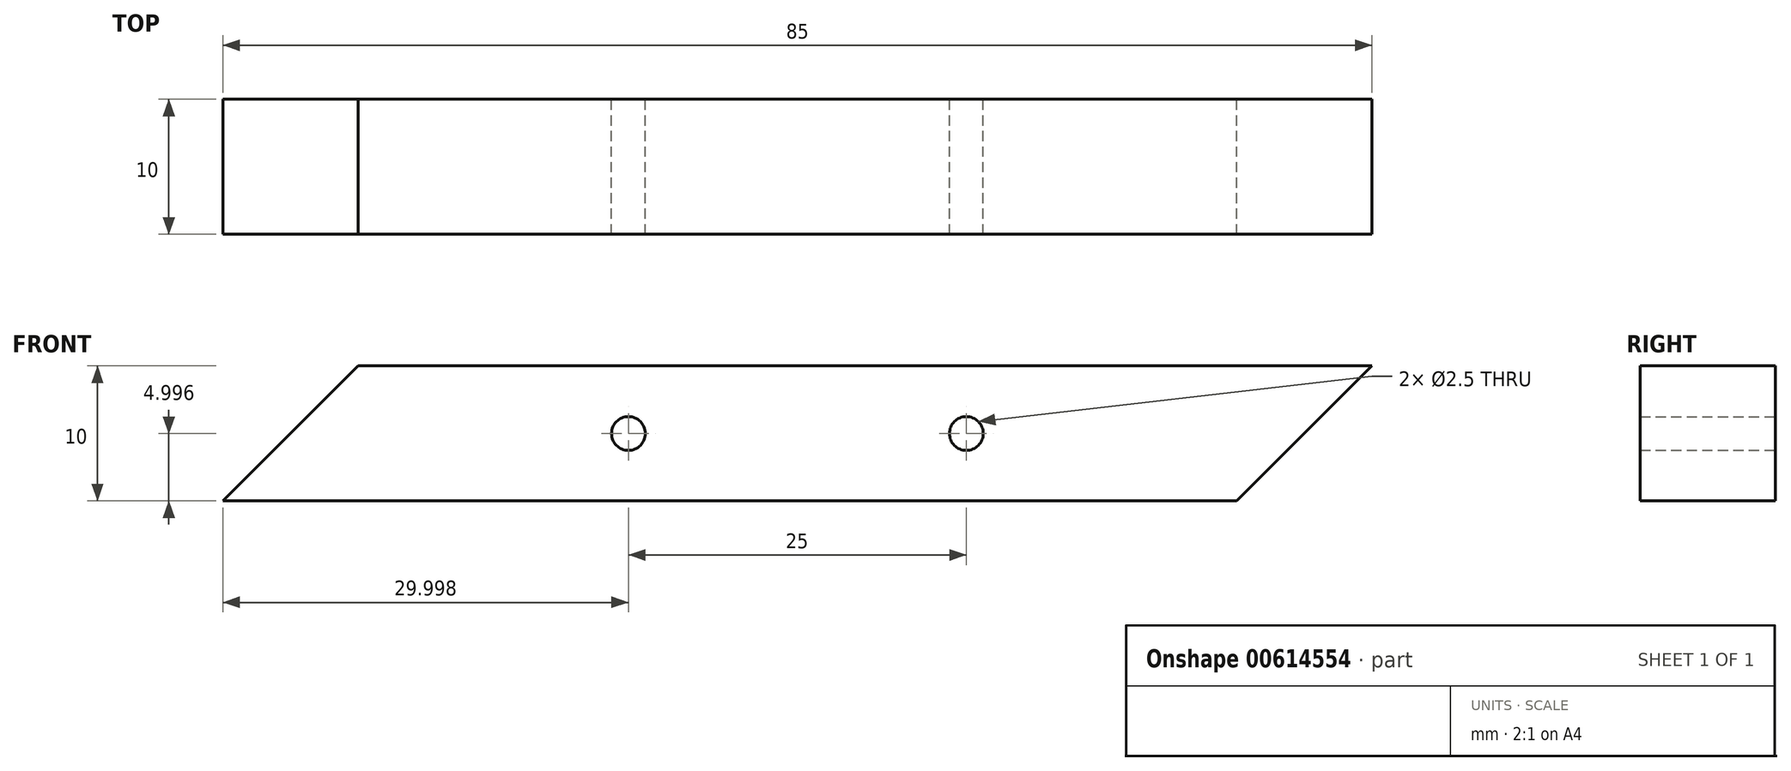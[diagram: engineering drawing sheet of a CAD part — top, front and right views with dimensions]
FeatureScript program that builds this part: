
annotation { "Feature Type Name" : "Feature", "Feature Type Description" : "" }
export const myFeature = defineFeature(function(context is Context, id is Id, definition is map)
    precondition{}
    {
        {
            var Q0;
            Q0=qCreatedBy(makeId("Front.planeOp"),FACE);
            var sketch = newSketch(context, id + "F0", { "sketchPlane" : qUnion([Q0])});
            skLineSegment(sketch, "E0.bottom", {"start": v(-26.1, 0.78) * mm, "end": v(38.9, 0.78) * mm});
            skLineSegment(sketch, "E1", {"start": v(-36.1, -9.22) * mm, "end": v(38.9, -9.22) * mm});
            skLineSegment(sketch, "E2", {"start": v(-36.1, -9.22) * mm, "end": v(-26.1, 0.78) * mm});
            skPoint(sketch, "E0.left.start.orphan", {"position": v(-36.1, 0.78) * mm});
            skLineSegment(sketch, "E3", {"start": v(38.9, -9.22) * mm, "end": v(48.9, 0.78) * mm});
            skLineSegment(sketch, "E4", {"start": v(48.9, 0.78) * mm, "end": v(38.9, 0.78) * mm});
            skCircle(sketch, "E5", {"center": v(-6.1, -4.22) * mm, "radius": 1.25 * mm});
            skCircle(sketch, "E6", {"center": v(18.9, -4.22) * mm, "radius": 1.25 * mm});
            skSolve(sketch);
        }
        {
            var Q0;
            Q0=makeQuery(id+"F0.imprint","IMPRINT",FACE,{"disambiguationData":[TD([[makeQuery(id+"F0.imprint","IMPRINT",EDGE,{"derivedFrom":sQuery(id+"F0.wireOp",EDGE,"E0.bottom")}),-1.0]])]});
            extrude(context, id + "F1", {"entities" : qUnion([Q0]), "endBound" : BoundingType.SYMMETRIC, "depth" : 10 * mm, "offsetDistance" : 25 * mm});
        }
        {
            var Q0;
            Q0=makeQuery(id+"F1.opExtrude","SWEPT_FACE",FACE,{"disambiguationData":[OSD([sQuery(id+"F0.wireOp",EDGE,"E2")])]});
            var sketch = newSketch(context, id + "F2", { "sketchPlane" : qUnion([Q0])});
            skCircle(sketch, "E7", {"center": v(-21.44, 0) * mm, "radius": 0.75 * mm});
            skSolve(sketch);
        }
        {
            var Q0;
            Q0=sQuery(id+"F2.wireOp",VERTEX,"E7.center");
            var Q1;
            Q1=makeQuery(id+"F1.opExtrude","SWEPT_BODY",BODY,{"disambiguationData":[OSD([sQuery(id+"F0.wireOp",EDGE,"E0.bottom"),sQuery(id+"F0.wireOp",EDGE,"E1"),sQuery(id+"F0.wireOp",EDGE,"E2"),sQuery(id+"F0.wireOp",EDGE,"E3"),sQuery(id+"F0.wireOp",EDGE,"E4"),sQuery(id+"F0.wireOp",EDGE,"E5"),sQuery(id+"F0.wireOp",EDGE,"E6")])]});
            hole(context, id + "F3", {"style" : HoleStyle.SIMPLE, "endStyle" : HoleEndStyle.BLIND, "holeDiameter" : 1.5 * mm, "majorDiameter" : 5 * mm, "holeDepth" : 5 * mm, "isTappedThrough" : true, "tappedDepth" : 12 * mm, "tapClearance" : 3, "locations" : qUnion([Q0]), "scope" : qUnion([Q1])});
        }
    });
